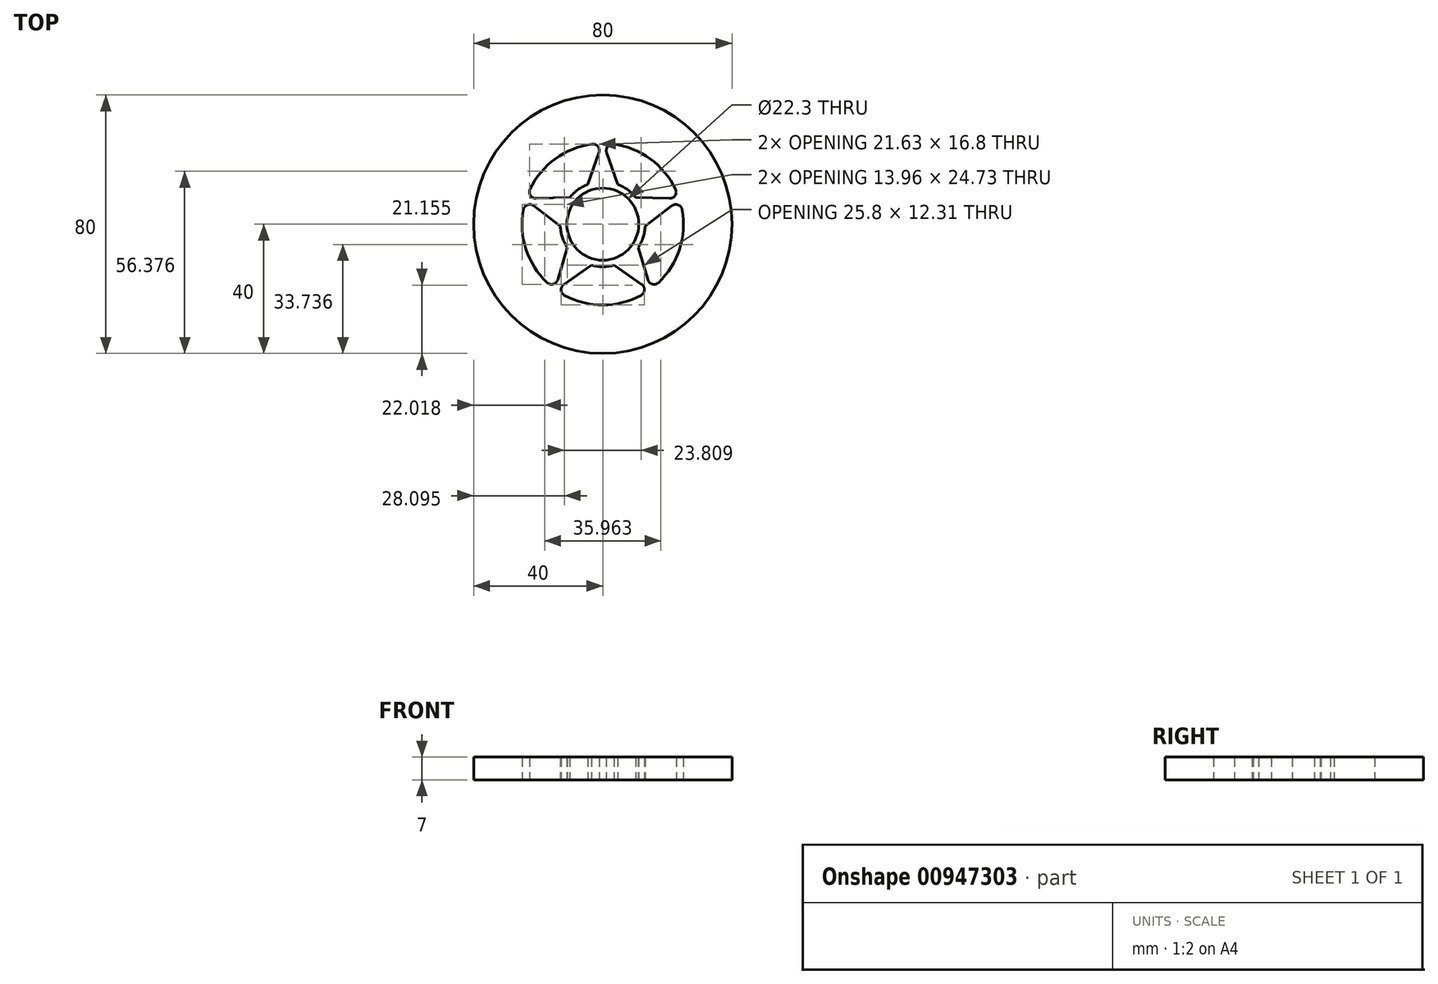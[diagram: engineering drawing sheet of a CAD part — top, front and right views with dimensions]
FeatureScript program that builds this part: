
annotation { "Feature Type Name" : "Feature", "Feature Type Description" : "" }
export const myFeature = defineFeature(function(context is Context, id is Id, definition is map)
    precondition{}
    {
        {
            var Q0;
            Q0=qCreatedBy(makeId("Top.planeOp"),FACE);
            var sketch = newSketch(context, id + "F0", { "sketchPlane" : qUnion([Q0])});
            skCircle(sketch, "E0", {"center": v(0, 0) * mm, "radius": 11.15 * mm});
            skCircle(sketch, "E1.0", {"center": v(0, 0) * mm, "radius": 13.15 * mm});
            skCircle(sketch, "E2", {"center": v(0, 0) * mm, "radius": 25 * mm});
            skLineSegment(sketch, "E3", {"start": v(0, 25.51) * mm, "end": v(-4.67, 12.3) * mm});
            skLineSegment(sketch, "E4", {"start": v(-4.67, 12.3) * mm, "end": v(4.67, 12.3) * mm});
            skLineSegment(sketch, "E5", {"start": v(4.67, 12.3) * mm, "end": v(0, 25.51) * mm});
            skLineSegment(sketch, "E6.1.0", {"start": v(-10.25, 8.24) * mm, "end": v(-24.26, 7.88) * mm});
            skLineSegment(sketch, "E6.1.1", {"start": v(-24.26, 7.88) * mm, "end": v(-13.13, -0.64) * mm});
            skLineSegment(sketch, "E6.1.2", {"start": v(-13.13, -0.64) * mm, "end": v(-10.25, 8.24) * mm});
            skLineSegment(sketch, "E6.2.0", {"start": v(-11, -7.2) * mm, "end": v(-15, -20.64) * mm});
            skLineSegment(sketch, "E6.2.1", {"start": v(-15, -20.64) * mm, "end": v(-3.45, -12.69) * mm});
            skLineSegment(sketch, "E6.2.2", {"start": v(-3.45, -12.69) * mm, "end": v(-11, -7.2) * mm});
            skLineSegment(sketch, "E6.3.0", {"start": v(3.45, -12.69) * mm, "end": v(15, -20.64) * mm});
            skLineSegment(sketch, "E6.3.1", {"start": v(15, -20.64) * mm, "end": v(11, -7.2) * mm});
            skLineSegment(sketch, "E6.3.2", {"start": v(11, -7.2) * mm, "end": v(3.45, -12.69) * mm});
            skLineSegment(sketch, "E6.4.0", {"start": v(13.13, -0.64) * mm, "end": v(24.26, 7.88) * mm});
            skLineSegment(sketch, "E6.4.1", {"start": v(24.26, 7.88) * mm, "end": v(10.25, 8.24) * mm});
            skLineSegment(sketch, "E6.4.2", {"start": v(10.25, 8.24) * mm, "end": v(13.13, -0.64) * mm});
            skCircle(sketch, "E7", {"center": v(0, 0) * mm, "radius": 30 * mm});
            skCircle(sketch, "E8", {"center": v(0, 0) * mm, "radius": 35 * mm});
            skCircle(sketch, "E9", {"center": v(0, 0) * mm, "radius": 40 * mm});
            skSolve(sketch);
        }
        {
            var Q0;
            Q0 = qSketchRegion(id + "F0", true);
            var Q1;
            Q1=makeQuery(id+"F0.imprint","IMPRINT",FACE,{"disambiguationData":[TD([[makeQuery(id+"F0.imprint","IMPRINT",EDGE,{"derivedFrom":sQuery(id+"F0.wireOp",EDGE,"E7")}),-1.0]])]});
            var Q2;
            {var subQ4=sQuery(id+"F0.wireOp",EDGE,"E5");var subQ6=sQuery(id+"F0.wireOp",EDGE,"E2");var subQ8=makeQuery(id+"F0.imprint","INTERSECT",VERTEX,{"derivedFrom":[subQ6,subQ4]});Q2=makeQuery(id+"F0.imprint","IMPRINT",FACE,{"disambiguationData":[TD([[makeQuery(id+"F0.imprint","IMPRINT",EDGE,{"disambiguationData":[TD([[subQ8,-1.0]])],"derivedFrom":subQ6}),1.0]])]});}
            var Q3;
            {var subQ1=sQuery(id+"F0.wireOp",EDGE,"E6.1.0");var subQ6=sQuery(id+"F0.wireOp",EDGE,"E2");var subQ8=makeQuery(id+"F0.imprint","INTERSECT",VERTEX,{"derivedFrom":[subQ6,subQ1]});Q3=makeQuery(id+"F0.imprint","IMPRINT",FACE,{"disambiguationData":[TD([[makeQuery(id+"F0.imprint","IMPRINT",EDGE,{"disambiguationData":[TD([[subQ8,-1.0]])],"derivedFrom":subQ6}),1.0]])]});}
            var Q4;
            {var subQ1=sQuery(id+"F0.wireOp",EDGE,"E6.2.0");var subQ6=sQuery(id+"F0.wireOp",EDGE,"E2");var subQ7=makeQuery(id+"F0.imprint","INTERSECT",VERTEX,{"derivedFrom":[subQ6,subQ1]});Q4=makeQuery(id+"F0.imprint","IMPRINT",FACE,{"disambiguationData":[TD([[makeQuery(id+"F0.imprint","IMPRINT",EDGE,{"disambiguationData":[TD([[subQ7,-1.0]])],"derivedFrom":subQ6}),1.0]])]});}
            var Q5;
            {var subQ1=sQuery(id+"F0.wireOp",EDGE,"E6.3.0");var subQ6=sQuery(id+"F0.wireOp",EDGE,"E2");var subQ7=makeQuery(id+"F0.imprint","INTERSECT",VERTEX,{"derivedFrom":[subQ6,subQ1]});Q5=makeQuery(id+"F0.imprint","IMPRINT",FACE,{"disambiguationData":[TD([[makeQuery(id+"F0.imprint","IMPRINT",EDGE,{"disambiguationData":[TD([[subQ7,-1.0]])],"derivedFrom":subQ6}),1.0]])]});}
            var Q6;
            Q6=makeQuery(id+"F0.imprint","IMPRINT",FACE,{"disambiguationData":[TD([[makeQuery(id+"F0.imprint","IMPRINT",EDGE,{"derivedFrom":sQuery(id+"F0.wireOp",EDGE,"E0")}),-1.0]])]});
            var Q7;
            {var subQ0=sQuery(id+"F0.wireOp",EDGE,"E4");Q7=makeQuery(id+"F0.imprint","IMPRINT",FACE,{"disambiguationData":[TD([[makeQuery(id+"F0.imprint","IMPRINT",EDGE,{"derivedFrom":subQ0}),1.0]])]});}
            var Q8;
            {var subQ0=sQuery(id+"F0.wireOp",EDGE,"E6.4.2");Q8=makeQuery(id+"F0.imprint","IMPRINT",FACE,{"disambiguationData":[TD([[makeQuery(id+"F0.imprint","IMPRINT",EDGE,{"derivedFrom":subQ0}),1.0]])]});}
            var Q9;
            {var subQ4=sQuery(id+"F0.wireOp",EDGE,"E6.4.1");var subQ6=sQuery(id+"F0.wireOp",EDGE,"E2");var subQ7=makeQuery(id+"F0.imprint","INTERSECT",VERTEX,{"derivedFrom":[subQ6,subQ4]});Q9=makeQuery(id+"F0.imprint","IMPRINT",FACE,{"disambiguationData":[TD([[makeQuery(id+"F0.imprint","IMPRINT",EDGE,{"disambiguationData":[TD([[subQ7,1.0]])],"derivedFrom":subQ6}),1.0]])]});}
            var Q10;
            {var subQ0=sQuery(id+"F0.wireOp",EDGE,"E6.3.2");Q10=makeQuery(id+"F0.imprint","IMPRINT",FACE,{"disambiguationData":[TD([[makeQuery(id+"F0.imprint","IMPRINT",EDGE,{"derivedFrom":subQ0}),1.0]])]});}
            var Q11;
            {var subQ0=sQuery(id+"F0.wireOp",EDGE,"E6.2.2");Q11=makeQuery(id+"F0.imprint","IMPRINT",FACE,{"disambiguationData":[TD([[makeQuery(id+"F0.imprint","IMPRINT",EDGE,{"derivedFrom":subQ0}),1.0]])]});}
            var Q12;
            {var subQ0=sQuery(id+"F0.wireOp",EDGE,"E6.1.2");Q12=makeQuery(id+"F0.imprint","IMPRINT",FACE,{"disambiguationData":[TD([[makeQuery(id+"F0.imprint","IMPRINT",EDGE,{"derivedFrom":subQ0}),1.0]])]});}
            var Q13;
            Q13=makeQuery(id+"F0.imprint","IMPRINT",FACE,{"disambiguationData":[TD([[makeQuery(id+"F0.imprint","IMPRINT",EDGE,{"derivedFrom":sQuery(id+"F0.wireOp",EDGE,"E7")}),1.0]])]});
            var Q14;
            {var subQ0=sQuery(id+"F0.wireOp",EDGE,"E6.1.0");var subQ1=sQuery(id+"F0.wireOp",EDGE,"E2");var subQ2=makeQuery(id+"F0.imprint","INTERSECT",VERTEX,{"derivedFrom":[subQ1,subQ0]});Q14=makeQuery(id+"F0.imprint","IMPRINT",FACE,{"disambiguationData":[TD([[makeQuery(id+"F0.imprint","IMPRINT",EDGE,{"disambiguationData":[TD([[subQ2,-1.0]])],"derivedFrom":subQ1}),-1.0]])]});}
            var Q15;
            {var subQ0=sQuery(id+"F0.wireOp",EDGE,"E6.2.0");var subQ1=sQuery(id+"F0.wireOp",EDGE,"E2");var subQ2=makeQuery(id+"F0.imprint","INTERSECT",VERTEX,{"derivedFrom":[subQ1,subQ0]});Q15=makeQuery(id+"F0.imprint","IMPRINT",FACE,{"disambiguationData":[TD([[makeQuery(id+"F0.imprint","IMPRINT",EDGE,{"disambiguationData":[TD([[subQ2,-1.0]])],"derivedFrom":subQ1}),-1.0]])]});}
            var Q16;
            {var subQ0=sQuery(id+"F0.wireOp",EDGE,"E6.3.0");var subQ1=sQuery(id+"F0.wireOp",EDGE,"E2");var subQ2=makeQuery(id+"F0.imprint","INTERSECT",VERTEX,{"derivedFrom":[subQ1,subQ0]});Q16=makeQuery(id+"F0.imprint","IMPRINT",FACE,{"disambiguationData":[TD([[makeQuery(id+"F0.imprint","IMPRINT",EDGE,{"disambiguationData":[TD([[subQ2,-1.0]])],"derivedFrom":subQ1}),-1.0]])]});}
            var Q17;
            {var subQ0=sQuery(id+"F0.wireOp",EDGE,"E6.4.1");var subQ1=sQuery(id+"F0.wireOp",EDGE,"E2");var subQ2=makeQuery(id+"F0.imprint","INTERSECT",VERTEX,{"derivedFrom":[subQ1,subQ0]});Q17=makeQuery(id+"F0.imprint","IMPRINT",FACE,{"disambiguationData":[TD([[makeQuery(id+"F0.imprint","IMPRINT",EDGE,{"disambiguationData":[TD([[subQ2,1.0]])],"derivedFrom":subQ1}),-1.0]])]});}
            var Q18;
            {var subQ0=sQuery(id+"F0.wireOp",EDGE,"E5");var subQ1=sQuery(id+"F0.wireOp",EDGE,"E2");var subQ2=makeQuery(id+"F0.imprint","INTERSECT",VERTEX,{"derivedFrom":[subQ1,subQ0]});Q18=makeQuery(id+"F0.imprint","IMPRINT",FACE,{"disambiguationData":[TD([[makeQuery(id+"F0.imprint","IMPRINT",EDGE,{"disambiguationData":[TD([[subQ2,-1.0]])],"derivedFrom":subQ1}),-1.0]])]});}
            extrude(context, id + "F1", {"entities" : qUnion([Q0, Q1, Q2, Q3, Q4, Q5, Q6, Q7, Q8, Q9, Q10, Q11, Q12, Q13, Q14, Q15, Q16, Q17, Q18]), "depth" : 7 * mm, "offsetDistance" : 25 * mm});
        }
        {
            var Q0;
            Q0=makeQuery(id+"F1.opExtrude","SWEPT_EDGE",EDGE,{"disambiguationData":[OSD([sQuery(id+"F0.wireOp",EDGE,"E2"),sQuery(id+"F0.wireOp",EDGE,"E5")])]});
            var Q1;
            Q1=makeQuery(id+"F1.opExtrude","SWEPT_EDGE",EDGE,{"disambiguationData":[OSD([sQuery(id+"F0.wireOp",EDGE,"E2"),sQuery(id+"F0.wireOp",EDGE,"E3")])]});
            var Q2;
            Q2=makeQuery(id+"F1.opExtrude","SWEPT_EDGE",EDGE,{"disambiguationData":[OSD([sQuery(id+"F0.wireOp",EDGE,"E2"),sQuery(id+"F0.wireOp",EDGE,"E6.4.1")])]});
            var Q3;
            Q3=makeQuery(id+"F1.opExtrude","SWEPT_EDGE",EDGE,{"disambiguationData":[OSD([sQuery(id+"F0.wireOp",EDGE,"E2"),sQuery(id+"F0.wireOp",EDGE,"E6.4.0")])]});
            var Q4;
            Q4=makeQuery(id+"F1.opExtrude","SWEPT_EDGE",EDGE,{"disambiguationData":[OSD([sQuery(id+"F0.wireOp",EDGE,"E2"),sQuery(id+"F0.wireOp",EDGE,"E6.3.1")])]});
            var Q5;
            Q5=makeQuery(id+"F1.opExtrude","SWEPT_EDGE",EDGE,{"disambiguationData":[OSD([sQuery(id+"F0.wireOp",EDGE,"E2"),sQuery(id+"F0.wireOp",EDGE,"E6.3.0")])]});
            var Q6;
            Q6=makeQuery(id+"F1.opExtrude","SWEPT_EDGE",EDGE,{"disambiguationData":[OSD([sQuery(id+"F0.wireOp",EDGE,"E2"),sQuery(id+"F0.wireOp",EDGE,"E6.2.1")])]});
            var Q7;
            Q7=makeQuery(id+"F1.opExtrude","SWEPT_EDGE",EDGE,{"disambiguationData":[OSD([sQuery(id+"F0.wireOp",EDGE,"E2"),sQuery(id+"F0.wireOp",EDGE,"E6.2.0")])]});
            var Q8;
            Q8=makeQuery(id+"F1.opExtrude","SWEPT_EDGE",EDGE,{"disambiguationData":[OSD([sQuery(id+"F0.wireOp",EDGE,"E2"),sQuery(id+"F0.wireOp",EDGE,"E6.1.1")])]});
            var Q9;
            Q9=makeQuery(id+"F1.opExtrude","SWEPT_EDGE",EDGE,{"disambiguationData":[OSD([sQuery(id+"F0.wireOp",EDGE,"E2"),sQuery(id+"F0.wireOp",EDGE,"E6.1.0")])]});
            fillet(context, id + "F2", {"entities" : qUnion([Q0, Q1, Q2, Q3, Q4, Q5, Q6, Q7, Q8, Q9]), "radius" : 2 * mm, "tangentPropagation" : true, "allowEdgeOverflow" : false});
        }
    });
